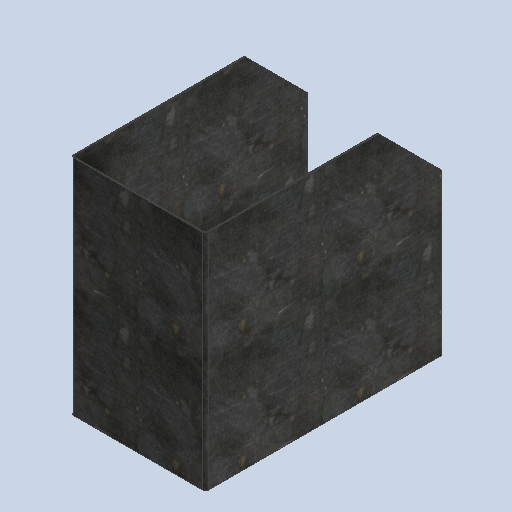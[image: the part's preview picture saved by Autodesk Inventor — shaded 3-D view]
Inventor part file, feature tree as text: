
AUTODESK INVENTOR PART (.ipt)
format: ipt  version: 2024.3 (Build 283343000, 343)  size: 462,336 bytes
history: native  units: mm
features: sheet_metal_op x9, sketch x6, other x6, projected_geometry x3, extrude x1
ambient origin geometry x8: Origin, YZ Plane, XZ Plane, XY Plane, X Axis, Y Axis, Z Axis, Center Point
bodies: Solid1 (feature_tree)
feature tree (25):
  sheet_metal_op  "Face1"
  sheet_metal_op  "Flange1"
  sheet_metal_op  "Flange2"
  sheet_metal_op  "Face2"
  extrude  "Extrusion1"  Depth=331.78mm
  sketch  "Sketch1"  dims[d0=350.0mm d1=331.78mm]
  other  "Plate1"
  sketch  "Sketch2"  dims[d2=239.261mm]
  other  "Plate2"
  sheet_metal_op  "Bend1"
  sheet_metal_op  "Corner1"
  sketch  "Sketch3"  dims[d3=45.0deg]
  other  "Plate3"
  sheet_metal_op  "Bend2"
  sheet_metal_op  "Corner2"
  sketch  "Sketch4"  dims[d4=2.0mm]
  sketch  "Sketch5"  dims[d5=2.0mm]
  projected_geometry  "Projected Loop1"
  projected_geometry  "Projected Loop2"
  other  "Plate4"
  sheet_metal_op  "Bend3"
  sketch  "Sketch6"  dims[d6=1.0mm d7=4.0mm d8=2.0mm d9=200.0mm d10=90.0deg d11=2.0mm d12=8.0mm d13=2.0mm d14=2.0mm d15=2.0mm d16=1.0mm d17=4.0mm d18=2.0mm d19=350.0mm d20=90.0deg d21=2.0mm d22=8.0mm d23=2.0mm d24=2.0mm d25=2.0mm d26=0.0mm d27=3.0mm d28=5.0mm d29=5.0mm d30=15.0mm d31=115.0mm d32=5.0mm d33=15.0mm d34=5.0mm d35=25.0mm d36=15.0mm d37=5.0mm d38=65.0mm d39=2.0mm d40=2.0mm d41=1.0mm d42=4.0mm d43=2.0mm d44=0.0mm d45=0.0mm]
  projected_geometry  "Projected Loop3"
  other  "Cut1"
  other  "Definition1"
